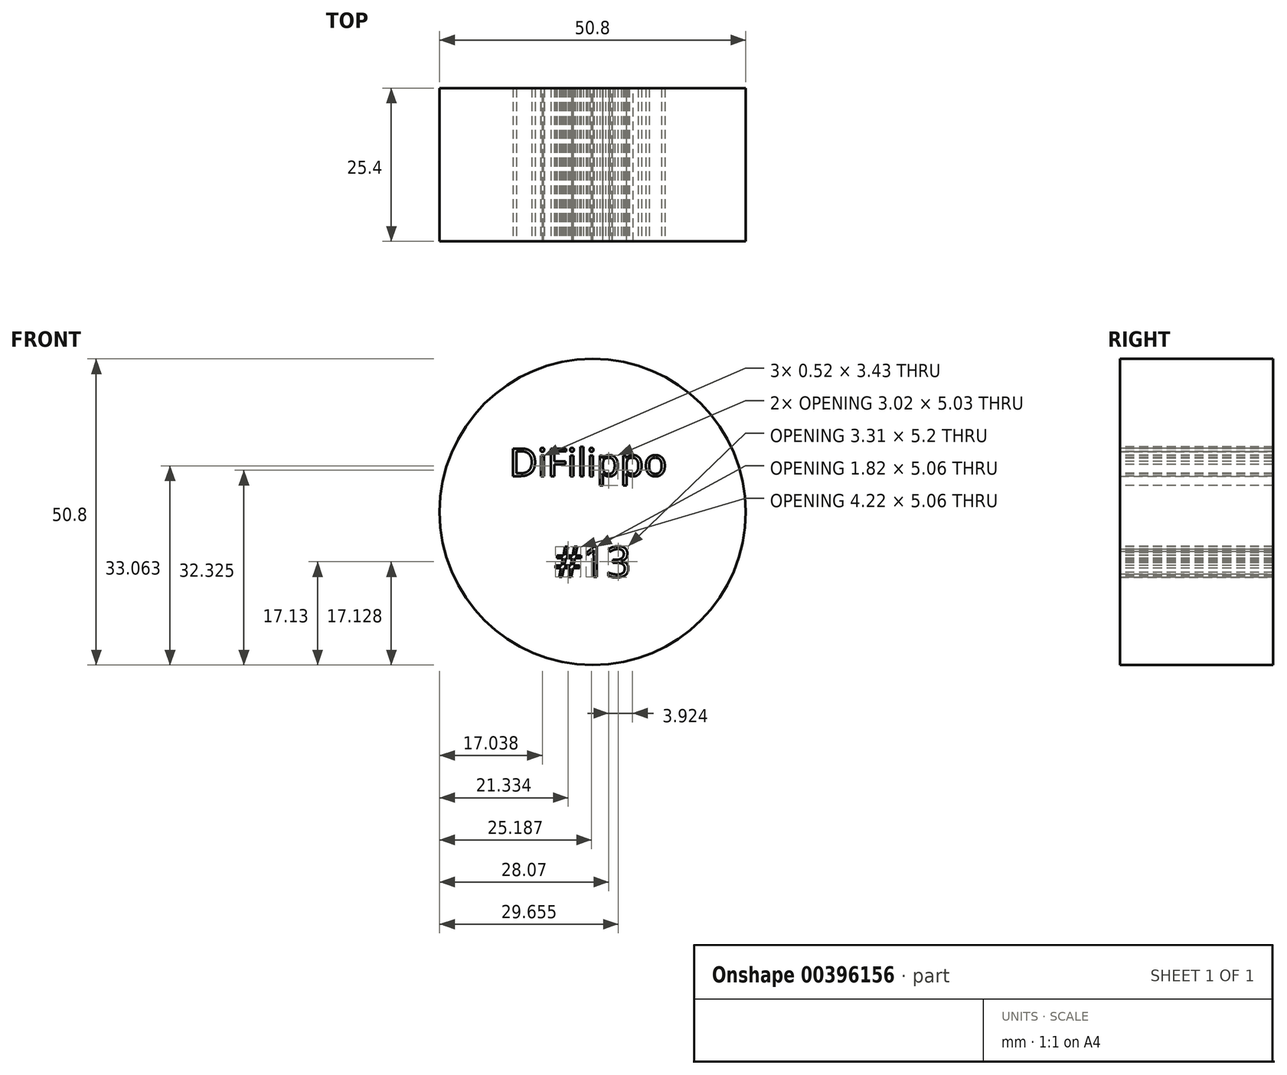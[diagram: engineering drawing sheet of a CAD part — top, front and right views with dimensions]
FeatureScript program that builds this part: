
annotation { "Feature Type Name" : "Feature", "Feature Type Description" : "" }
export const myFeature = defineFeature(function(context is Context, id is Id, definition is map)
    precondition{}
    {
        {
            var Q0;
            Q0=qCreatedBy(makeId("Front.planeOp"),FACE);
            var sketch = newSketch(context, id + "F0", { "sketchPlane" : qUnion([Q0])});
            skCircle(sketch, "E0", {"center": v(28.24, 15.85) * mm, "radius": 25.4 * mm});
            skSolve(sketch);
        }
        {
            var Q0;
            Q0=makeQuery(id+"F0.imprint","IMPRINT",FACE,{"disambiguationData":[TD([[makeQuery(id+"F0.imprint","IMPRINT",EDGE,{"derivedFrom":sQuery(id+"F0.wireOp",EDGE,"E0")}),1.0]])]});
            extrude(context, id + "F1", {"entities" : qUnion([Q0]), "depth" : 25.4 * mm});
        }
        {
            var Q0;
            Q0=makeQuery(id+"F1.opExtrude","CAP_FACE",FACE,{"disambiguationData":[OSD([sQuery(id+"F0.wireOp",EDGE,"E0")])],"isStart":false});
            var sketch = newSketch(context, id + "F2", { "sketchPlane" : qUnion([Q0])});
            skText(sketch, "E1", { "text": "DiFilippo", "fontName": "OpenSans-Regular.ttf"});
            const initialGuessF2  = {"E1": [0.0144, 0.0218, 1, 0, 0.00461]};
            skSetInitialGuess(sketch, initialGuessF2);
            skSolve(sketch);
        }
        {
            var Q0;
            {var subQ0=sQuery(id+"F0.wireOp",EDGE,"E0");Q0=makeQuery(id+"FVVd9eyRJQSXN62_1.boolean.opBoolean","SPLIT",FACE,{"disambiguationData":[TD([makeQuery(id+"F1.opExtrude","SWEPT_FACE",FACE,{"disambiguationData":[OSD([subQ0])]})])],"derivedFrom":makeQuery(id+"F1.opExtrude","CAP_FACE",FACE,{"disambiguationData":[OSD([subQ0])],"isStart":false})});}
            var sketch = newSketch(context, id + "F3", { "sketchPlane" : qUnion([Q0])});
            skText(sketch, "E2", { "text": "#13", "fontName": "OpenSans-Regular.ttf"});
            const initialGuessF3  = {"E2": [0.02189, 0.00505, 1, 0, 0.0051]};
            skSetInitialGuess(sketch, initialGuessF3);
            skSolve(sketch);
        }
        {
            var Q0;
            Q0 = qSketchRegion(id + "F3", true);
            extrude(context, id + "F4", {"entities" : qUnion([Q0]), "operationType" : NewBodyOperationType.REMOVE, "oppositeDirection" : true, "depth" : 25.4 * mm});
        }
        {
            var Q0;
            Q0 = qSketchRegion(id + "F2", true);
            extrude(context, id + "F5", {"entities" : qUnion([Q0]), "operationType" : NewBodyOperationType.REMOVE, "oppositeDirection" : true, "depth" : 25.4 * mm});
        }
    });
